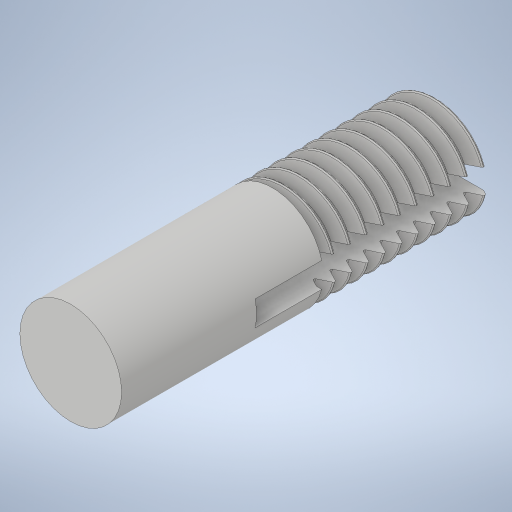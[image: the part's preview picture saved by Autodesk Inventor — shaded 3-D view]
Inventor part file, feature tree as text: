
AUTODESK INVENTOR PART (.ipt)
format: ipt  version: 2023 (Build 270158000, 158)  size: 921,600 bytes
history: native  units: mm
features: sketch x5, extrude x2, revolve x2, thread x1, helix x1, boolean_combine x1
ambient origin geometry x8: Origin, YZ Plane, XZ Plane, XY Plane, X Axis, Y Axis, Z Axis, Center Point
bodies: Solid1 (feature_tree), Solid2 (feature_tree)
feature tree (12):
  extrude  "Extrusion1"  Depth=22.1mm TaperAngle=0.0deg
  thread  "Thread1"  [1 undecoded]
  revolve  "Revolution1"  [1 undecoded]
  revolve  "Revolution2"  [1 undecoded]
  helix  "Coil1"  [1 undecoded]
  sketch  "Sketch5"  dims[d25=14.0mm d26=0.0mm d27=8.0mm d28=0.5mm d29=0.872665mm d30=0.5mm d31=0.872665mm]
  boolean_combine  "Combine1"
  extrude  "Extrusion2"  Depth=1.5mm
  sketch  "Sketch1"  dims[d0=6.1mm d1=22.1mm d2=0.0mm d3=10.0mm d4=0.0mm]
  sketch  "Sketch2"  dims[d5=9.599311mm d6=0.160083mm d7=0.160083mm d10=1.0mm]
  sketch  "Sketch3"  dims[d12=9.599311mm d14=0.0mm d15=0.0mm]
  sketch  "Sketch4"  dims[d16=1.001mm d17=12.0mm d18=10.0mm d19=0.0mm d20=0.0mm d21=0.0mm d22=0.0mm d23=0.0mm d24=1.5mm]
note: 4 required parameter values undecoded (feature->parameter linkage not recoverable at this tier; creation-order binding heuristic only, values carry confidence <= 0.55)